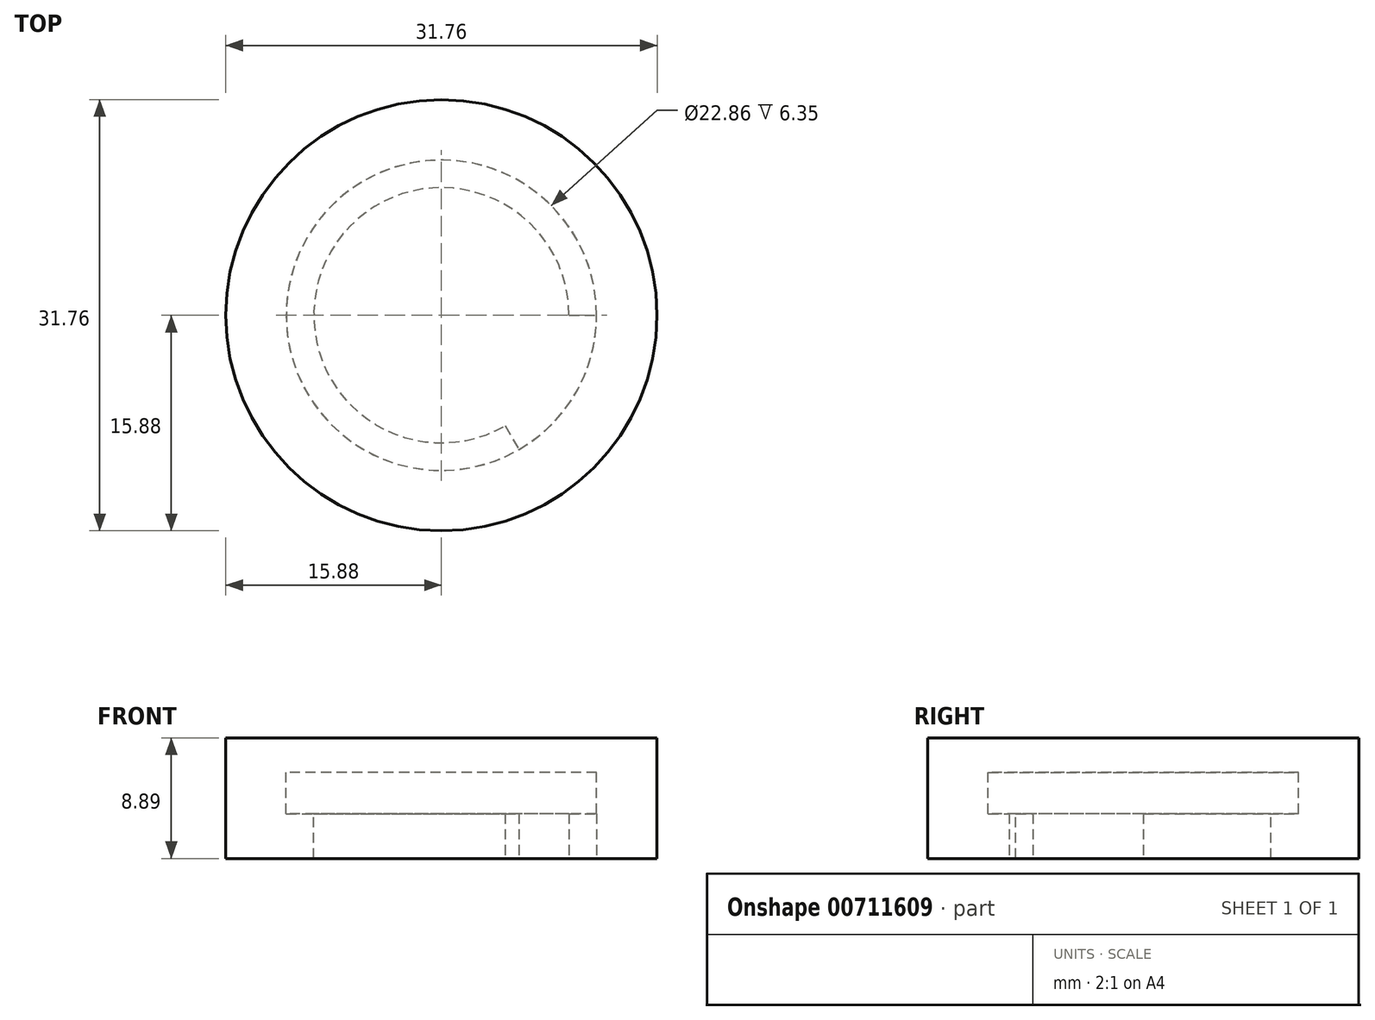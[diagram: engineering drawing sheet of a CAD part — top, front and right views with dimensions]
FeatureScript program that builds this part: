
annotation { "Feature Type Name" : "Feature", "Feature Type Description" : "" }
export const myFeature = defineFeature(function(context is Context, id is Id, definition is map)
    precondition{}
    {
        {
            var Q0;
            Q0=qCreatedBy(makeId("Top.planeOp"),FACE);
            var sketch = newSketch(context, id + "F0", { "sketchPlane" : qUnion([Q0])});
            skCircle(sketch, "E0", {"center": v(0, 0) * mm, "radius": 15.88 * mm});
            skSolve(sketch);
        }
        {
            var Q0;
            Q0 = qSketchRegion(id + "F0", true);
            extrude(context, id + "F1", {"entities" : qUnion([Q0]), "depth" : 8.9 * mm, "offsetDistance" : 25.4 * mm});
        }
        {
            var Q0;
            Q0=qCreatedBy(makeId("Front.planeOp"),FACE);
            var sketch = newSketch(context, id + "F2", { "sketchPlane" : qUnion([Q0])});
            skLineSegment(sketch, "E1", {"start": v(0, 6.35) * mm, "end": v(11.43, 6.35) * mm});
            skLineSegment(sketch, "E2", {"start": v(11.43, 6.35) * mm, "end": v(11.43, 3.3) * mm});
            skLineSegment(sketch, "E3", {"start": v(11.43, 3.3) * mm, "end": v(9.4, 3.3) * mm});
            skLineSegment(sketch, "E4", {"start": v(9.4, 3.3) * mm, "end": v(9.4, 0) * mm});
            skLineSegment(sketch, "E5", {"start": v(9.4, 0) * mm, "end": v(0, 0) * mm});
            skLineSegment(sketch, "E6", {"start": v(0, 0) * mm, "end": v(0, 6.35) * mm});
            skSolve(sketch);
        }
        {
            var Q0;
            Q0 = qSketchRegion(id + "F2", true);
            var Q1;
            Q1=sQuery(id+"F2.wireOp",EDGE,"E6");
            revolve(context, id + "F3", {"operationType" : NewBodyOperationType.REMOVE, "surfaceOperationType" : NewSurfaceOperationType.NEW, "entities" : qUnion([Q0]), "axis" : qUnion([Q1]), "revolveType" : RevolveType.FULL, "oppositeDirection" : true});
        }
        {
            var Q0;
            Q0=qCreatedBy(makeId("Front.planeOp"),FACE);
            var sketch = newSketch(context, id + "F4", { "sketchPlane" : qUnion([Q0])});
            skLineSegment(sketch, "E7.bottom", {"start": v(9.4, 3.3) * mm, "end": v(11.43, 3.3) * mm});
            skLineSegment(sketch, "E7.top", {"start": v(9.4, 0) * mm, "end": v(11.43, 0) * mm});
            skLineSegment(sketch, "E7.left", {"start": v(9.4, 3.3) * mm, "end": v(9.4, 0) * mm});
            skLineSegment(sketch, "E7.right", {"start": v(11.43, 3.3) * mm, "end": v(11.43, 0) * mm});
            skLineSegment(sketch, "E8", {"start": v(0, 0) * mm, "end": v(0, 4) * mm, "construction": true});
            skSolve(sketch);
        }
        {
            var Q0;
            Q0 = qSketchRegion(id + "F4", true);
            var Q1;
            Q1=sQuery(id+"F2.wireOp",EDGE,"E6");
            revolve(context, id + "F5", {"operationType" : NewBodyOperationType.REMOVE, "surfaceOperationType" : NewSurfaceOperationType.NEW, "entities" : qUnion([Q0]), "axis" : qUnion([Q1]), "revolveType" : RevolveType.ONE_DIRECTION, "oppositeDirection" : true, "angle" : 60 * degree});
        }
    });
